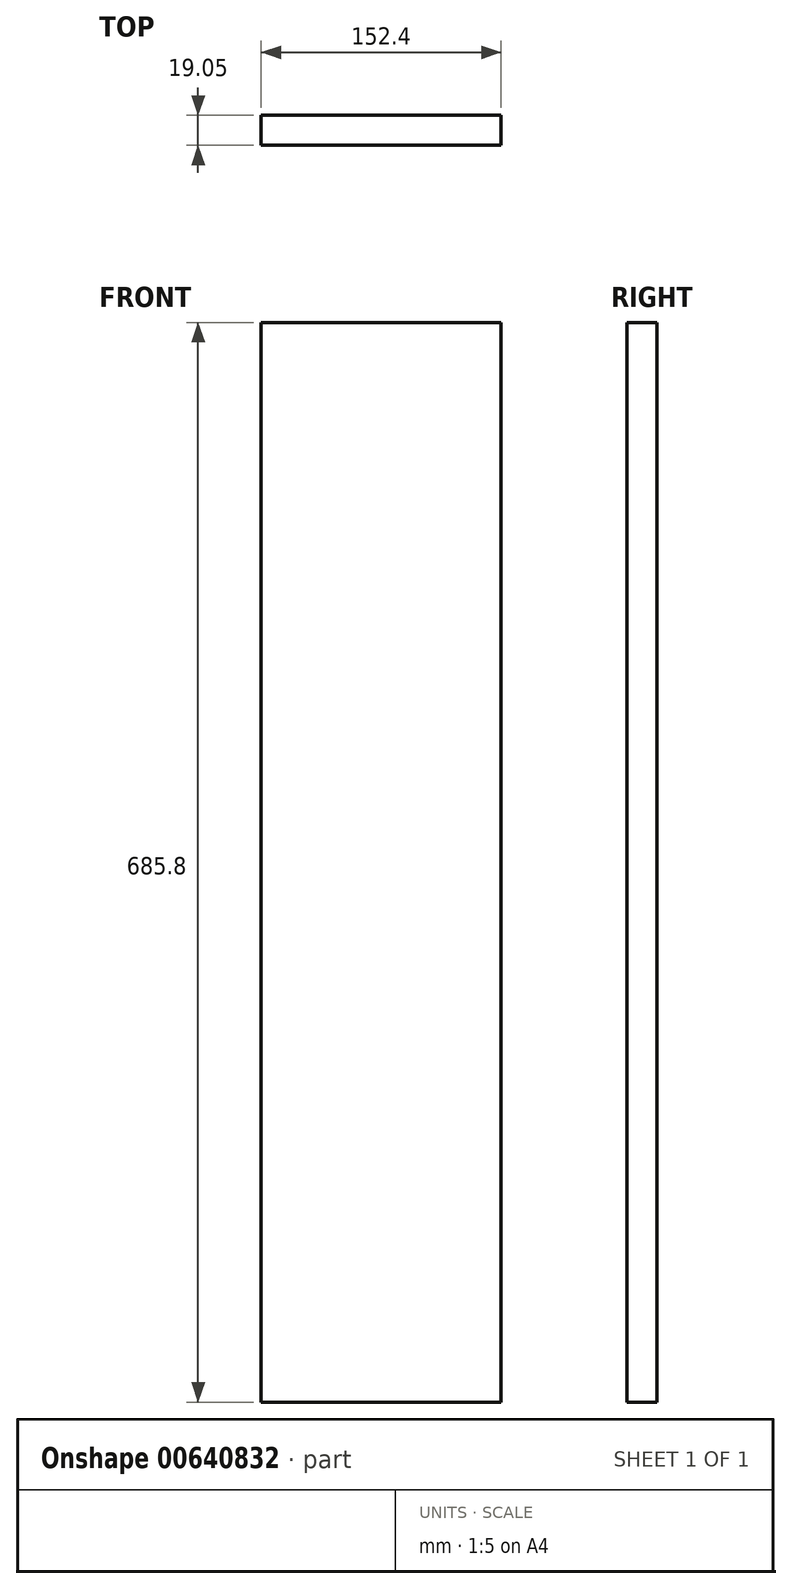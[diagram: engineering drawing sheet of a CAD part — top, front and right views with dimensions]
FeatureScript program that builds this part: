
annotation { "Feature Type Name" : "Feature", "Feature Type Description" : "" }
export const myFeature = defineFeature(function(context is Context, id is Id, definition is map)
    precondition{}
    {
        {
            var Q0;
            Q0=qCreatedBy(makeId("Front.planeOp"),FACE);
            var sketch = newSketch(context, id + "F0", { "sketchPlane" : qUnion([Q0])});
            skLineSegment(sketch, "E0.bottom", {"start": v(76.2, 342.9) * mm, "end": v(-76.2, 342.9) * mm});
            skLineSegment(sketch, "E0.top", {"start": v(76.2, -342.9) * mm, "end": v(-76.2, -342.9) * mm});
            skLineSegment(sketch, "E0.left", {"start": v(76.2, 342.9) * mm, "end": v(76.2, -342.9) * mm});
            skLineSegment(sketch, "E0.right", {"start": v(-76.2, 342.9) * mm, "end": v(-76.2, -342.9) * mm});
            skPoint(sketch, "E0.middle", {"position": v(0, 0) * mm});
            skSolve(sketch);
        }
        {
            var Q0;
            Q0=makeQuery(id+"F0.imprint","IMPRINT",FACE,{"disambiguationData":[TD([[makeQuery(id+"F0.imprint","IMPRINT",EDGE,{"derivedFrom":sQuery(id+"F0.wireOp",EDGE,"E0.bottom")}),1.0]])]});
            extrude(context, id + "F1", {"entities" : qUnion([Q0]), "depth" : 19.05 * mm, "offsetDistance" : 25.4 * mm});
        }
    });
